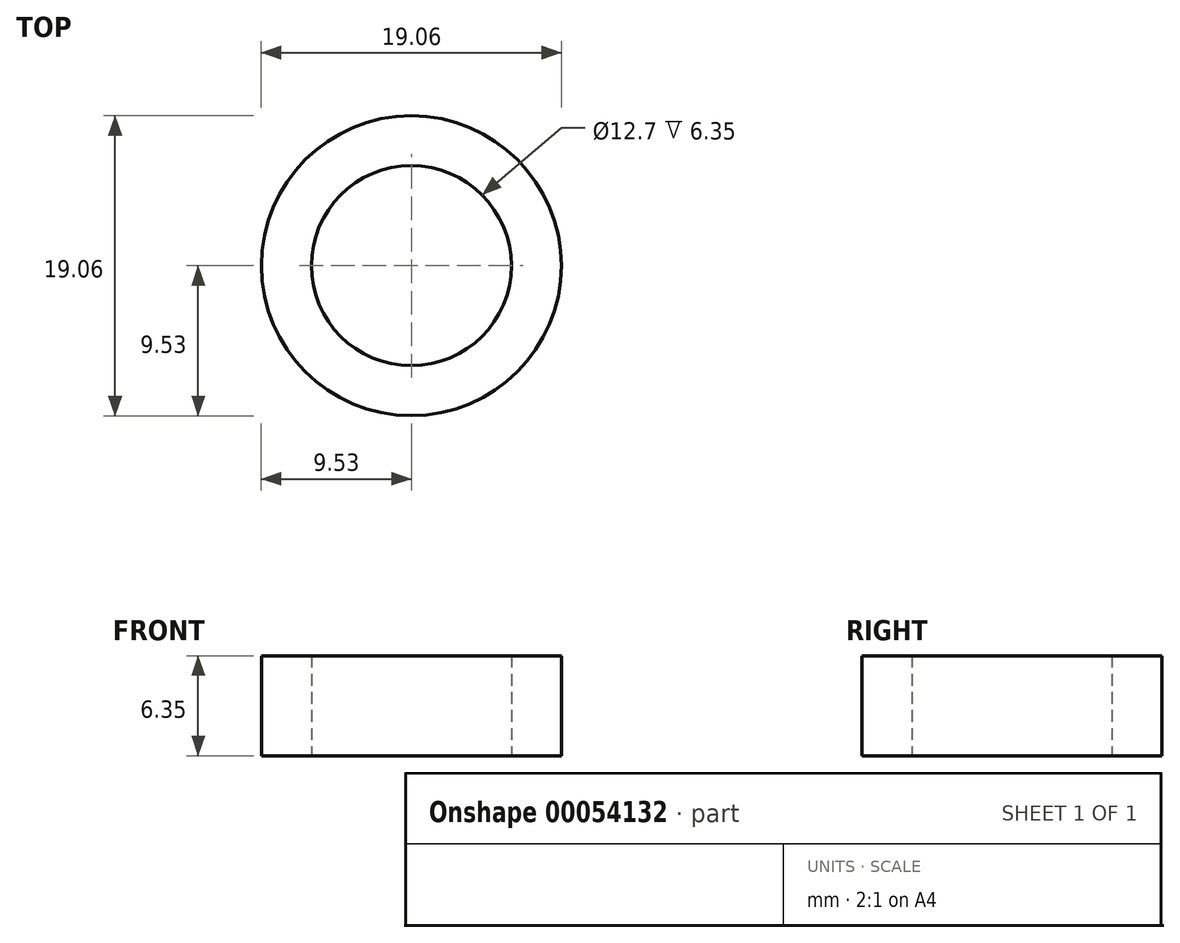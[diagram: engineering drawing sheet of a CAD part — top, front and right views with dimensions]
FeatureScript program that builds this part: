
annotation { "Feature Type Name" : "Feature", "Feature Type Description" : "" }
export const myFeature = defineFeature(function(context is Context, id is Id, definition is map)
    precondition{}
    {
        {
            var Q0;
            Q0=qCreatedBy(makeId("Top.planeOp"),FACE);
            var sketch = newSketch(context, id + "F0", { "sketchPlane" : qUnion([Q0])});
            skCircle(sketch, "E0", {"center": v(0, 0) * mm, "radius": 9.53 * mm});
            skCircle(sketch, "E1", {"center": v(0, 0) * mm, "radius": 6.35 * mm});
            skSolve(sketch);
        }
        {
            var Q0;
            Q0 = qSketchRegion(id + "F0", true);
            extrude(context, id + "F1", {"entities" : qUnion([Q0]), "depth" : 5 * mm});
        }
        {
            var Q0;
            Q0 = qSketchRegion(id + "F0", true);
            extrude(context, id + "F2", {"entities" : qUnion([Q0]), "operationType" : NewBodyOperationType.ADD, "depth" : 6.35 * mm});
        }
    });
